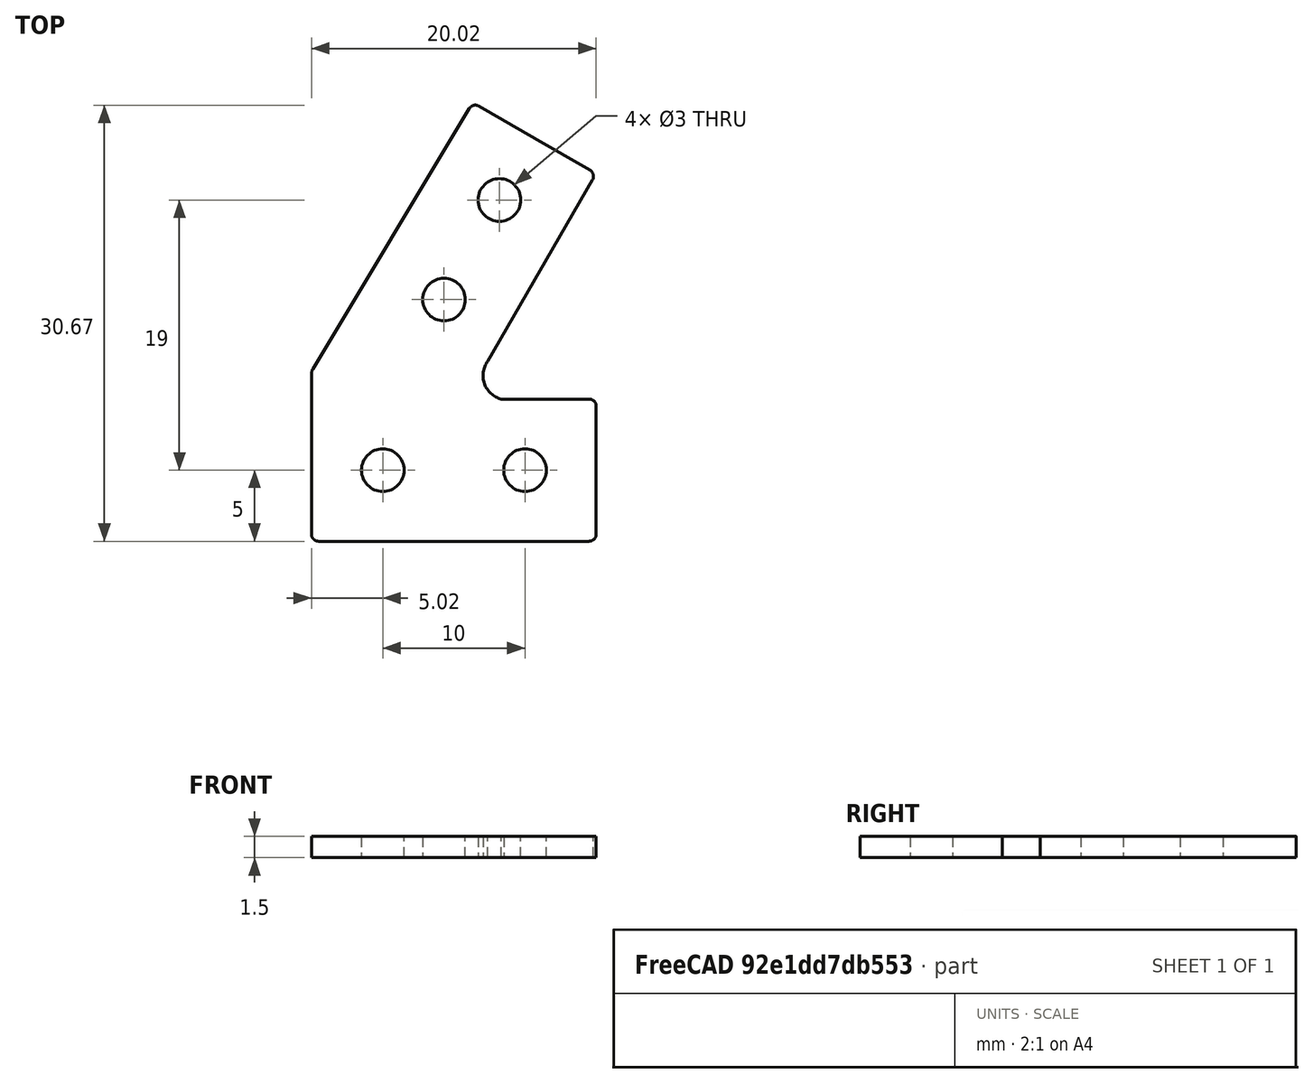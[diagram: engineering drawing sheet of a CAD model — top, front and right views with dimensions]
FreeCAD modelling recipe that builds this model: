
FCSTD DOCUMENT  (FreeCAD 0.18R16146 (Git))
Label: makerbeam_bracket_60degree
License: All rights reserved
LicenseURL: http://en.wikipedia.org/wiki/All_rights_reserved
objects: Sketcher::SketchObject×1, PartDesign::Pad×1, PartDesign::Fillet×1, PartDesign::Body×1
note: 5 computed .brp shape members not serialized (recipe doc carries the construction recipe); baked Part::Feature solids carry a one-line shape summary decoded from their .brp

FEATURE [Sketcher::SketchObject] Sketch
  MapMode = 5
  Support = -> [XY_Plane]
  sketch-geometry (13):
    g0: Circle CenterX=-5 CenterY=5 CenterZ=0 NormalX=0 NormalY=0 NormalZ=1 AngleXU=0 Radius=1.5
    g1: Circle CenterX=-15 CenterY=5 CenterZ=0 NormalX=0 NormalY=0 NormalZ=1 AngleXU=0 Radius=1.5
    g2: Circle CenterX=-10.7 CenterY=17 CenterZ=0 NormalX=0 NormalY=0 NormalZ=1 AngleXU=0 Radius=1.5
    g3: Circle CenterX=-6.8 CenterY=24 CenterZ=0 NormalX=0 NormalY=0 NormalZ=1 AngleXU=0 Radius=1.5
    g4: LineSegment StartX=0 StartY=0 StartZ=0 EndX=-20.0251 EndY=0 EndZ=0
    g5: LineSegment StartX=-20.0251 StartY=0 StartZ=0 EndX=-20 EndY=12 EndZ=0
    g6: LineSegment StartX=0 StartY=0 StartZ=0 EndX=0 EndY=10 EndZ=0
    g7: LineSegment StartX=0 StartY=10 StartZ=0 EndX=-6.67064 EndY=10 EndZ=0
    g8: LineSegment StartX=-4.33405 StartY=28.3496 StartZ=0 EndX=-8.66418 EndY=30.8496 EndZ=0
    g9: LineSegment StartX=-0.00392453 StartY=25.8496 StartZ=0 EndX=-4.33405 EndY=28.3496 EndZ=0
    g10: LineSegment StartX=-8.66418 StartY=30.8496 StartZ=0 EndX=-20 EndY=12 EndZ=0
    g11: LineSegment StartX=-0.00392453 StartY=25.8496 StartZ=0 EndX=-7.6189 EndY=12.6601 EndZ=0
    g12: ArcOfCircle CenterX=-6.2649 CenterY=11.6437 CenterZ=0 NormalX=0 NormalY=0 NormalZ=1 AngleXU=0 Radius=1.69303 StartAngle=2.49767 EndAngle=4.47038
  constraints (26):
    c: DistanceX(g0,g-1) = 5
    c: DistanceY(g-1,g0) = 5
    c: DistanceX(g1,g-1) = 15
    c: DistanceX(g2,g-1) = 10.7
    c: DistanceY(g-1,g2) = 17
    c: DistanceX(g3,g-1) = 6.8
    c: DistanceY(g-1,g3) = 24
    c: Coincident(g-1,g4)
    c: PointOnObject(g4,g-1)
    c: Coincident(g4,g5)
    c: Coincident(g4,g6)
    c: PointOnObject(g6,g-2)
    c: Coincident(g6,g7)
    c: Horizontal(g7)
    c: Angle(g8) = 2.61799
    c: Distance(g8) = 5
    c: Distance(g3,g8) = 5
    c: Parallel(g8,g9) = 2.61799
    c: Equal(g8,g9) = 5
    c: Coincident(g9,g8)
    c: Coincident(g10,g8)
    c: Coincident(g10,g5)
    c: Coincident(g11,g9)
    c: Angle(g7,g11) = 1.0472
    c: Coincident(g11,g12)
    c: Coincident(g12,g7)
FEATURE [PartDesign::Pad] Pad
  Length = 1.5
  Length2 = 100
  Profile = -> Sketch
  Type = 0
FEATURE [PartDesign::Fillet] Fillet
  Base = -> Pad [Edge14,Edge17,Edge1,Edge8,Edge11,Edge20]
  BaseFeature = -> Pad
  Radius = 0.5
FEATURE [PartDesign::Body] Body  label="makerbeam_bracket_60degree"
  Group = -> [Sketch,Pad,Fillet]
  Origin = -> Origin
  Tip = -> Fillet
